# Revit family: Hager-Vector-IP65-UV_Resistance-syst-BE-fr
name_source: partatom
category: Electrical Equipment
units: mm (PartAtom-declared; Revit-internal decimal feet)

## family parameters
Cut with Voids When Loaded = No
Host = Face
Panel Configuration = Two Columns, Circuits Across
Part Type = Panelboard
Room Calculation Point = No
Round Connector Dimension = Use Diameter
Shared = No

## types (13) — shared parameters
EF000003 - mode de pose = EV000384 - saillie
EF000007 - couleur = EV000270 - gris
EF000116 - numéro RAL = 7035
EF000118 - avec cadre/support de montage = No
EF000339 - type de capot = EV004216 - porte
EF001062 - finition CEM = No
EF001088 - possibilité de montage en saillie = Yes
EF001134 - rail DIN = Yes
EF001596 - matériau du boîtier/corps = EV000139 - plastique
EF004462 - type de fermeture = EV000154 - autre
EF005474 - indice de protection (IP) = EV006421 - IP65
EF006244 - couvercle/porte transparent(e) = Yes
EF006306 - avec serrure = No
EF009212 - finition du couvercle = EV000116 - fermé
EF015776 - borne de mise à la terre = No
EF015777 - borne à conducteur neutre = No
EF015941 - porte pour transmission du signal = Yes
HG000001 - nombre de colonnes = 1
HG000002 - avec porte = Yes
HG000003 - Gamme = Vector
HG000005 - Epaisseur = 3 mm  [stored 0.00984252 ft]
HG000006 - Encastré = No
HG000009 - Porte à double battant = No
HG000010 - Portes asymétriques = No
HG000011 - Rangées du bas vides = No
HG000017 - Distance entre pôles = 18 mm  [stored 0.0590551 ft]
Manufacturer = Hager
Type Comments = Vector
zero-valued in all types: Default Elevation, EF000218 - profondeur d'encastrement, EF000332 - hauteur d'encastrement, EF000846 - largeur d'encastrement, HG000007 - Nombre de colonnes vides, HG000008 - Nombre de rangées vides

## per-type parameters (varying)
| type | EF000008 - largeur | EF000040 - hauteur | EF000049 - profondeur | EF000266 - nombre de rangées | EF001131 - profondeur intérieure | EF002950 - largeur en nombre de modules | HG000004 - Référence fabricant | Model |
| Saillie IP65 L111 H175 P93 3 Modules - VE103PN | 111 mm | 175 mm | 93 mm | 1 | 93 mm | 3 | VE103PN | VE103PN |
| Saillie IP65 L165 H190 P113 6 Modules - VE106PN | 165 mm | 190 mm | 113 mm | 1 | 113 mm | 6 | VE106PN | VE106PN |
| Saillie IP65 L237 H210 P114 10 Modules - VE110PN | 237 mm | 210 mm | 114 mm | 1 | 114 mm | 10 | VE110PN | VE110PN |
| Saillie IP65 L310 H302 P151 12 Modules - VE112DN | 310 mm | 302 mm | 151 mm  [stored 0.495407 ft] | 1 | 151 mm  [stored 0.495407 ft] | 12 | VE112DN | VE112DN |
| Saillie IP65 L310 H302 P151 12 Modules - VE112PN | 310 mm | 302 mm | 151 mm  [stored 0.495407 ft] | 1 | 151 mm  [stored 0.495407 ft] | 12 | VE112PN | VE112PN |
| Saillie IP65 L310 H427 P151 12 Modules - VE212DN | 310 mm | 427 mm | 151 mm  [stored 0.495407 ft] | 2 | 151 mm  [stored 0.495407 ft] | 12 | VE212DN | VE212DN |
| Saillie IP65 L310 H427 P151 12 Modules - VE212PN | 310 mm | 427 mm | 151 mm  [stored 0.495407 ft] | 2 | 151 mm  [stored 0.495407 ft] | 12 | VE212PN | VE212PN |
| Saillie IP65 L310 H552 P151 12 Modules - VE312DN | 310 mm | 552 mm | 151 mm  [stored 0.495407 ft] | 3 | 151 mm  [stored 0.495407 ft] | 12 | VE312DN | VE312DN |
| Saillie IP65 L310 H552 P151 12 Modules - VE312PN | 310 mm | 552 mm | 151 mm  [stored 0.495407 ft] | 3 | 151 mm  [stored 0.495407 ft] | 12 | VE312PN | VE312PN |
| Saillie IP65 L310 H677 P151 12 Modules - VE412PN | 310 mm | 677 mm | 151 mm  [stored 0.495407 ft] | 4 | 151 mm  [stored 0.495407 ft] | 12 | VE412PN | VE412PN |
| Saillie IP65 L418 H302 P151 18 Modules - VE118PN | 418 mm  [stored 1.37139 ft] | 302 mm | 151 mm  [stored 0.495407 ft] | 1 | 151 mm  [stored 0.495407 ft] | 18 | VE118PN | VE118PN |
| Saillie IP65 L418 H452 P151 18 Modules - VE218PN | 418 mm  [stored 1.37139 ft] | 452 mm | 151 mm  [stored 0.495407 ft] | 2 | 151 mm  [stored 0.495407 ft] | 18 | VE218PN | VE218PN |
| Saillie IP65 L418 H602 P151 18 Modules - VE318PN | 418 mm  [stored 1.37139 ft] | 602 mm  [stored 1.97507 ft] | 151 mm  [stored 0.495407 ft] | 3 | 151 mm  [stored 0.495407 ft] | 18 | VE318PN | VE318PN |

note: [stored X ft] marks values corroborated as IEEE doubles in the binary element streams (Revit-internal decimal feet)

## geometry (parser evidence)
native form markers: Sweep x17
no freeform markers — native parametric forms only
